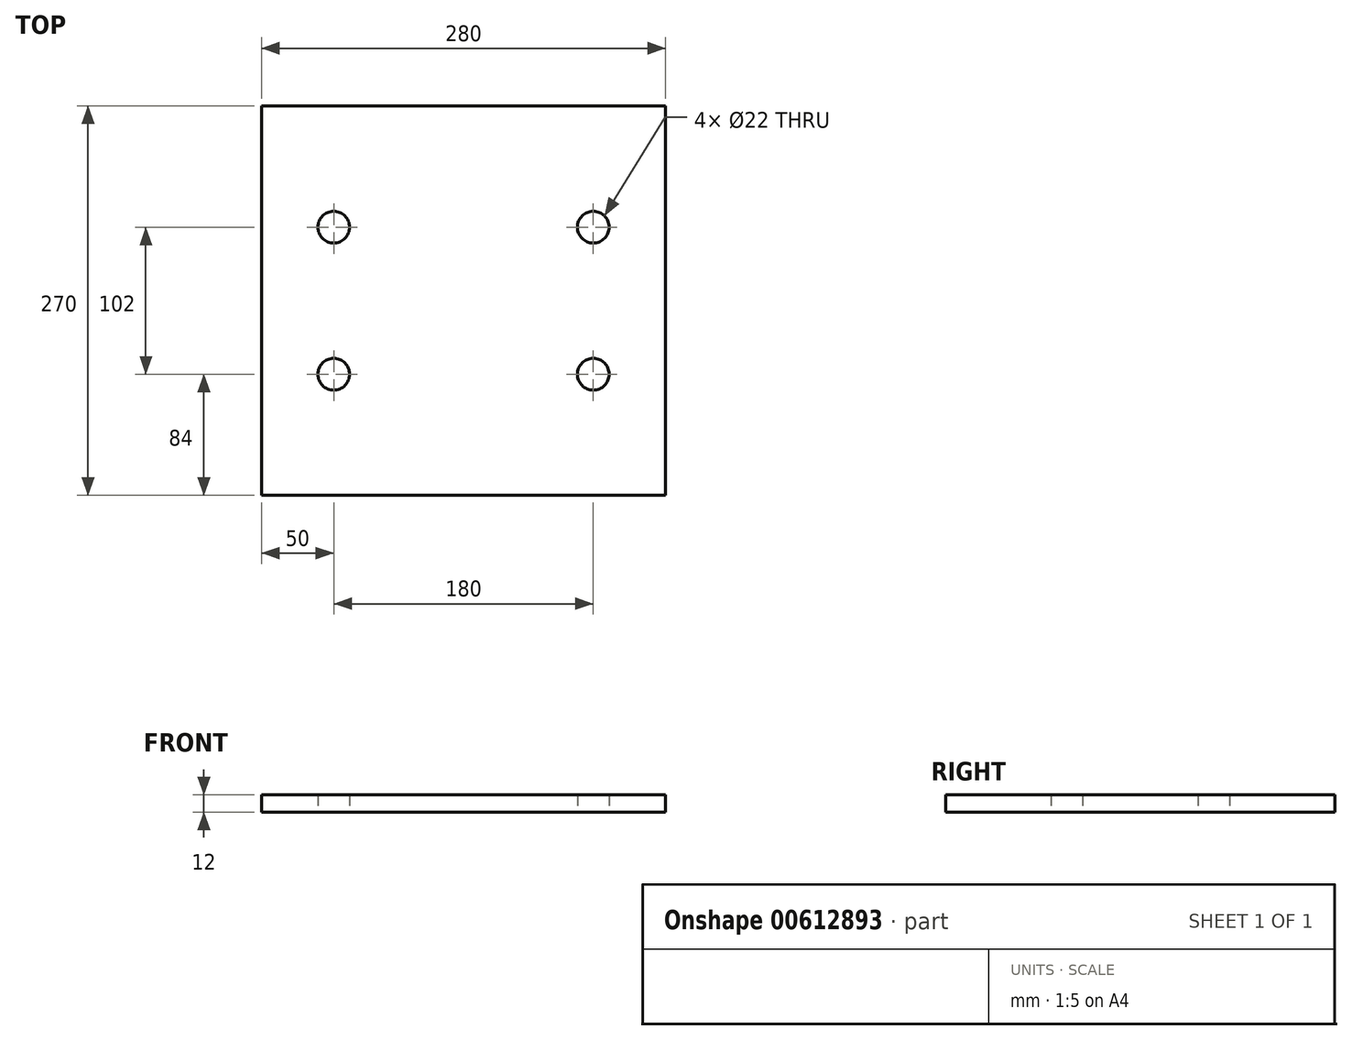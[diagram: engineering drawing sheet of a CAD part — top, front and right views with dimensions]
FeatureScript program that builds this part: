
annotation { "Feature Type Name" : "Feature", "Feature Type Description" : "" }
export const myFeature = defineFeature(function(context is Context, id is Id, definition is map)
    precondition{}
    {
        {
            var Q0;
            Q0=qCreatedBy(makeId("Top.planeOp"),FACE);
            var sketch = newSketch(context, id + "F0", { "sketchPlane" : qUnion([Q0])});
            skLineSegment(sketch, "E0.bottom", {"start": v(140, 135) * mm, "end": v(-140, 135) * mm});
            skLineSegment(sketch, "E0.top", {"start": v(140, -135) * mm, "end": v(-140, -135) * mm});
            skLineSegment(sketch, "E0.left", {"start": v(140, 135) * mm, "end": v(140, -135) * mm});
            skLineSegment(sketch, "E0.right", {"start": v(-140, 135) * mm, "end": v(-140, -135) * mm});
            skPoint(sketch, "E0.middle", {"position": v(0, 0) * mm});
            skCircle(sketch, "E1", {"center": v(-90, 51) * mm, "radius": 11 * mm});
            skCircle(sketch, "E2", {"center": v(90, 51) * mm, "radius": 11 * mm});
            skCircle(sketch, "E3", {"center": v(-90, -51) * mm, "radius": 11 * mm});
            skCircle(sketch, "E4", {"center": v(90, -51) * mm, "radius": 11 * mm});
            skSolve(sketch);
        }
        {
            var Q0;
            Q0=makeQuery(id+"F0.imprint","IMPRINT",FACE,{"disambiguationData":[TD([[makeQuery(id+"F0.imprint","IMPRINT",EDGE,{"derivedFrom":sQuery(id+"F0.wireOp",EDGE,"E0.bottom")}),1.0]])]});
            extrude(context, id + "F1", {"entities" : qUnion([Q0]), "endBound" : BoundingType.SYMMETRIC, "depth" : 12 * mm, "offsetDistance" : 25 * mm});
        }
    });
